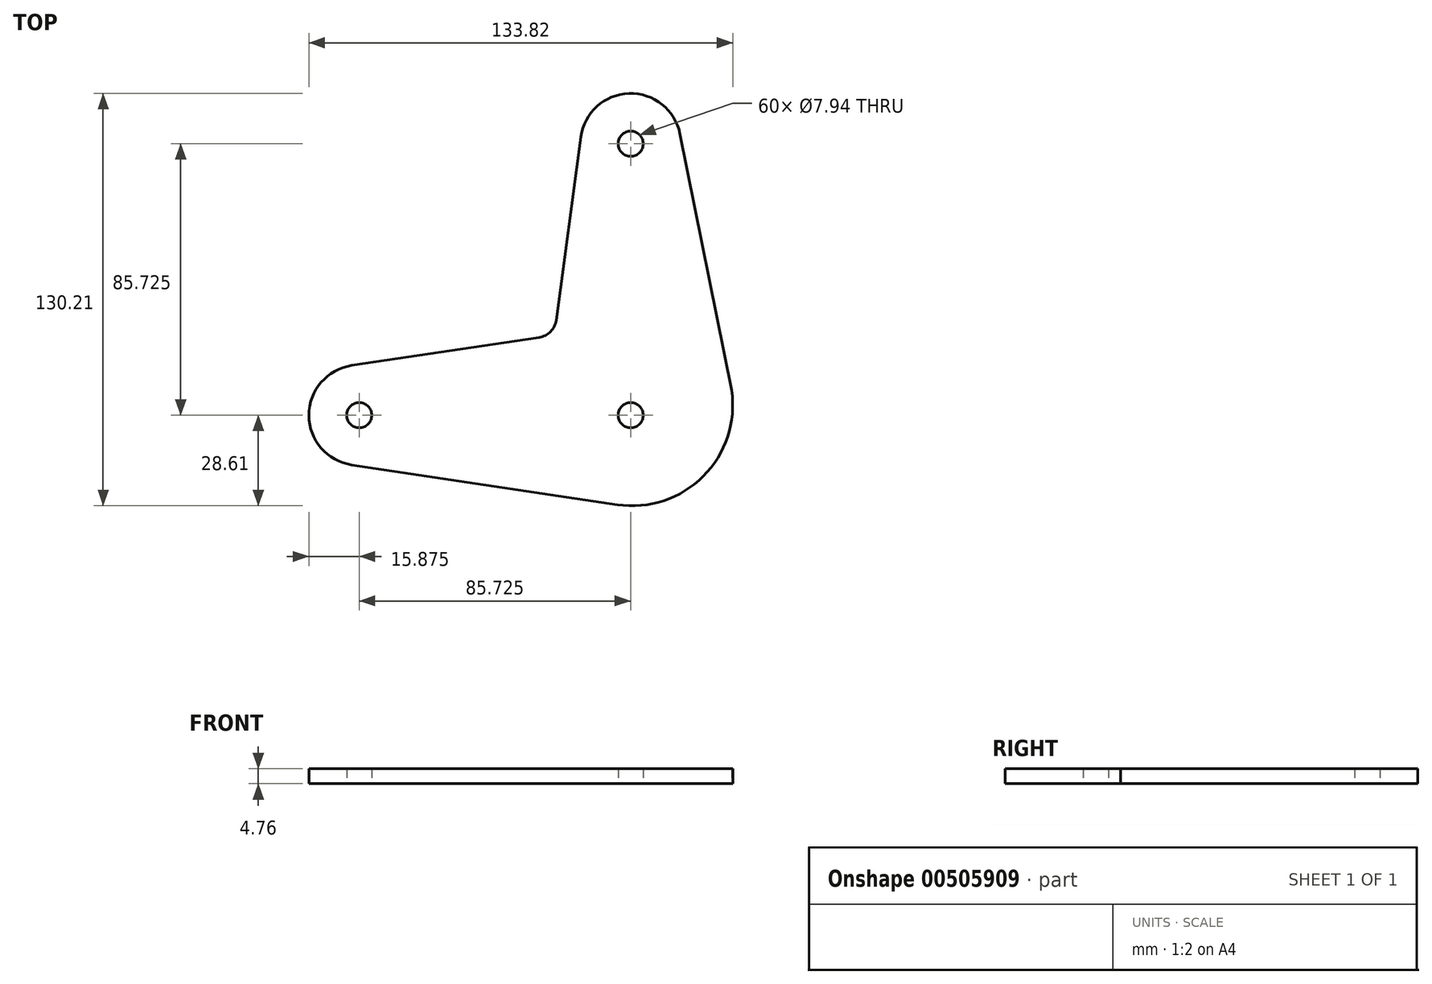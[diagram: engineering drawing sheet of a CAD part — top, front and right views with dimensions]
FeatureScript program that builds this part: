
annotation { "Feature Type Name" : "Feature", "Feature Type Description" : "" }
export const myFeature = defineFeature(function(context is Context, id is Id, definition is map)
    precondition{}
    {
        {
            var Q0;
            Q0=qCreatedBy(makeId("Top.planeOp"),FACE);
            var sketch = newSketch(context, id + "F0", { "sketchPlane" : qUnion([Q0])});
            skLineSegment(sketch, "E0", {"start": v(0, 0) * mm, "end": v(-146.78, 0) * mm, "construction": true});
            skLineSegment(sketch, "E1", {"start": v(0, 0) * mm, "end": v(0, 97.2) * mm, "construction": true});
            skArc(sketch, "E2", {"start": v(15.56, 88.86) * mm, "mid": v(-0.51, 101.6) * mm, "end": v(-15.73, 87.85) * mm});
            skArc(sketch, "E3", {"start": v(-88.08, 15.7) * mm, "mid": v(-101.6, 0) * mm, "end": v(-88.08, -15.7) * mm});
            skCircle(sketch, "E4", {"center": v(0, 85.73) * mm, "radius": 3.97 * mm});
            skCircle(sketch, "E5", {"center": v(0, 0) * mm, "radius": 3.97 * mm});
            skCircle(sketch, "E6", {"center": v(-85.73, 0) * mm, "radius": 3.97 * mm});
            skLineSegment(sketch, "E7", {"start": v(31.87, 7.84) * mm, "end": v(15.56, 88.86) * mm});
            skLineSegment(sketch, "E8", {"start": v(-4.23, -28.26) * mm, "end": v(-88.08, -15.7) * mm});
            skLineSegment(sketch, "E9", {"start": v(-24.17, 25.27) * mm, "end": v(-88.08, 15.7) * mm});
            skLineSegment(sketch, "E10", {"start": v(-24.17, 25.27) * mm, "end": v(-15.73, 87.85) * mm});
            skArc(sketch, "E11.trimOffspring", {"start": v(-4.23, -28.26) * mm, "mid": v(22.92, -19.31) * mm, "end": v(31.87, 7.84) * mm});
            skSolve(sketch);
        }
        {
            var Q0;
            Q0 = qSketchRegion(id + "F0", true);
            extrude(context, id + "F1", {"entities" : qUnion([Q0]), "depth" : 4.76 * mm});
        }
        {
            var Q0;
            Q0=makeQuery(id+"F1.opExtrude","SWEPT_EDGE",EDGE,{"disambiguationData":[OSD([sQuery(id+"F0.wireOp",EDGE,"a87NuGwc-VF6o-IFGJ-aGIg-MwW1pmW3PEEA"),sQuery(id+"F0.wireOp",EDGE,"lkQKnBeE-EAV9-fM9n-1QMc-3fY0z7bfAscB")])]});
            var Q1;
            Q1=makeQuery(id+"F1.opExtrude","SWEPT_EDGE",EDGE,{"disambiguationData":[OSD([sQuery(id+"F0.wireOp",EDGE,"E9"),sQuery(id+"F0.wireOp",EDGE,"E10")])]});
            fillet(context, id + "F2", {"entities" : qUnion([Q0, Q1]), "radius" : 6.35 * mm, "tangentPropagation" : true, "allowEdgeOverflow" : false});
        }
    });
